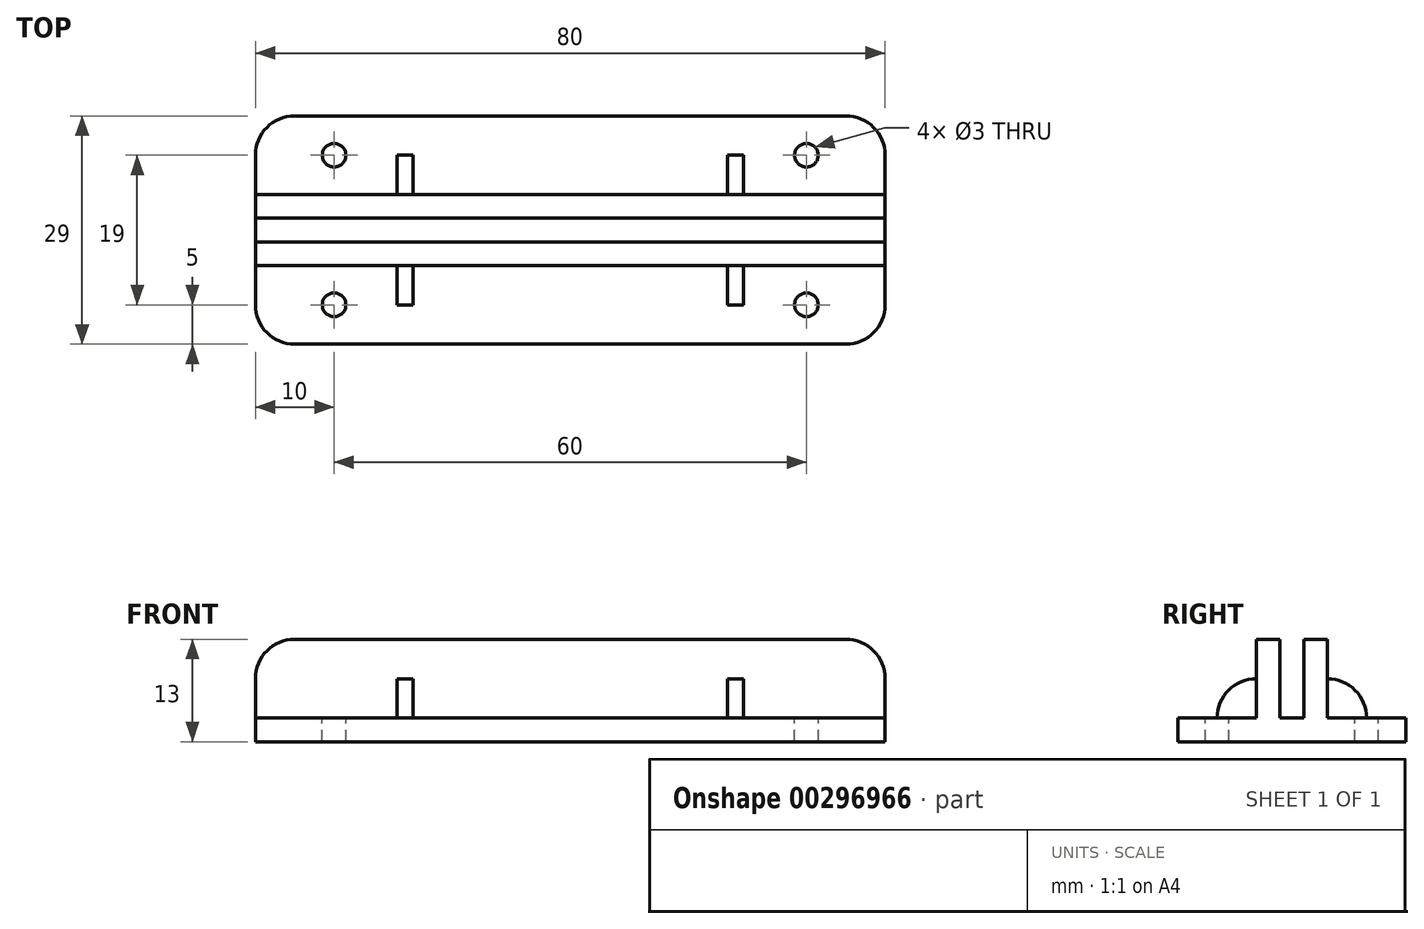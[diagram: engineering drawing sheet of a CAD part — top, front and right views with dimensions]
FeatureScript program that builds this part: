
annotation { "Feature Type Name" : "Feature", "Feature Type Description" : "" }
export const myFeature = defineFeature(function(context is Context, id is Id, definition is map)
    precondition{}
    {
        {
            var Q0;
            Q0=qCreatedBy(makeId("Top.planeOp"),FACE);
            var sketch = newSketch(context, id + "F0", { "sketchPlane" : qUnion([Q0])});
            skLineSegment(sketch, "E0.bottom", {"start": v(-40, 14.5) * mm, "end": v(40, 14.5) * mm});
            skLineSegment(sketch, "E0.top", {"start": v(-40, -14.5) * mm, "end": v(40, -14.5) * mm});
            skLineSegment(sketch, "E0.left", {"start": v(-40, 14.5) * mm, "end": v(-40, -14.5) * mm});
            skLineSegment(sketch, "E0.right", {"start": v(40, 14.5) * mm, "end": v(40, -14.5) * mm});
            skSolve(sketch);
        }
        {
            var Q0;
            Q0=makeQuery(id+"F0.imprint","IMPRINT",FACE,{"disambiguationData":[TD([[makeQuery(id+"F0.imprint","IMPRINT",EDGE,{"derivedFrom":sQuery(id+"F0.wireOp",EDGE,"E0.bottom")}),-1.0]])]});
            extrude(context, id + "F1", {"entities" : qUnion([Q0]), "depth" : 3 * mm});
        }
        {
            var Q0;
            Q0=makeQuery(id+"F1.opExtrude","CAP_FACE",FACE,{"disambiguationData":[OSD([sQuery(id+"F0.wireOp",EDGE,"E0.bottom"),sQuery(id+"F0.wireOp",EDGE,"E0.top"),sQuery(id+"F0.wireOp",EDGE,"E0.left"),sQuery(id+"F0.wireOp",EDGE,"E0.right")])],"isStart":false});
            var sketch = newSketch(context, id + "F2", { "sketchPlane" : qUnion([Q0])});
            skLineSegment(sketch, "E1.bottom", {"start": v(-40, 4.5) * mm, "end": v(40, 4.5) * mm});
            skLineSegment(sketch, "E1.top", {"start": v(-40, 1.5) * mm, "end": v(40, 1.5) * mm});
            skLineSegment(sketch, "E1.left", {"start": v(-40, 4.5) * mm, "end": v(-40, 1.5) * mm});
            skLineSegment(sketch, "E1.right", {"start": v(40, 4.5) * mm, "end": v(40, 1.5) * mm});
            skLineSegment(sketch, "E2.MirrorCS", {"start": v(40, -4.5) * mm, "end": v(40, -1.5) * mm});
            skLineSegment(sketch, "E3.MirrorCS", {"start": v(-40, -4.5) * mm, "end": v(-40, -1.5) * mm});
            skLineSegment(sketch, "E4.MirrorCS", {"start": v(-40, -1.5) * mm, "end": v(40, -1.5) * mm});
            skLineSegment(sketch, "E5.MirrorCS", {"start": v(-40, -4.5) * mm, "end": v(40, -4.5) * mm});
            skSolve(sketch);
        }
        {
            var Q0;
            Q0=makeQuery(id+"F2.imprint","IMPRINT",FACE,{"disambiguationData":[TD([[makeQuery(id+"F2.imprint","IMPRINT",EDGE,{"derivedFrom":sQuery(id+"F2.wireOp",EDGE,"E1.bottom")}),-1.0]])]});
            var Q1;
            Q1=makeQuery(id+"F2.imprint","IMPRINT",FACE,{"disambiguationData":[TD([[makeQuery(id+"F2.imprint","IMPRINT",EDGE,{"derivedFrom":sQuery(id+"F2.wireOp",EDGE,"E2.MirrorCS")}),-1.0]])]});
            extrude(context, id + "F3", {"entities" : qUnion([Q0, Q1]), "operationType" : NewBodyOperationType.ADD, "depth" : 10 * mm});
        }
        {
            var Q0;
            Q0=makeQuery(id+"F1.opExtrude","SWEPT_EDGE",EDGE,{"disambiguationData":[OSD([sQuery(id+"F0.wireOp",EDGE,"E0.bottom"),sQuery(id+"F0.wireOp",EDGE,"E0.right")])]});
            var Q1;
            Q1=makeQuery(id+"F1.opExtrude","SWEPT_EDGE",EDGE,{"disambiguationData":[OSD([sQuery(id+"F0.wireOp",EDGE,"E0.top"),sQuery(id+"F0.wireOp",EDGE,"E0.right")])]});
            var Q2;
            Q2=makeQuery(id+"F1.opExtrude","SWEPT_EDGE",EDGE,{"disambiguationData":[OSD([sQuery(id+"F0.wireOp",EDGE,"E0.bottom"),sQuery(id+"F0.wireOp",EDGE,"E0.left")])]});
            var Q3;
            Q3=makeQuery(id+"F1.opExtrude","SWEPT_EDGE",EDGE,{"disambiguationData":[OSD([sQuery(id+"F0.wireOp",EDGE,"E0.top"),sQuery(id+"F0.wireOp",EDGE,"E0.left")])]});
            var Q4;
            Q4=makeQuery(id+"F3.opExtrude","CAP_EDGE",EDGE,{"disambiguationData":[OSD([sQuery(id+"F2.wireOp",EDGE,"E1.right")])],"isStart":false});
            var Q5;
            Q5=makeQuery(id+"F3.opExtrude","CAP_EDGE",EDGE,{"disambiguationData":[OSD([sQuery(id+"F2.wireOp",EDGE,"E2.MirrorCS")])],"isStart":false});
            var Q6;
            Q6=makeQuery(id+"F3.opExtrude","CAP_EDGE",EDGE,{"disambiguationData":[OSD([sQuery(id+"F2.wireOp",EDGE,"E1.left")])],"isStart":false});
            var Q7;
            Q7=makeQuery(id+"F3.opExtrude","CAP_EDGE",EDGE,{"disambiguationData":[OSD([sQuery(id+"F2.wireOp",EDGE,"E3.MirrorCS")])],"isStart":false});
            fillet(context, id + "F4", {"entities" : qUnion([Q0, Q1, Q2, Q3, Q4, Q5, Q6, Q7]), "radius" : 5 * mm, "tangentPropagation" : true, "allowEdgeOverflow" : false});
        }
        {
            var Q0;
            {var subQ0=sQuery(id+"F0.wireOp",EDGE,"E0.left");var subQ1=sQuery(id+"F0.wireOp",EDGE,"E0.right");var subQ2=sQuery(id+"F0.wireOp",EDGE,"E0.bottom");Q0=makeQuery(id+"F3.boolean.opBoolean","SPLIT",FACE,{"disambiguationData":[TD([makeQuery(id+"F1.opExtrude","SWEPT_FACE",FACE,{"disambiguationData":[OSD([subQ2])]})])],"derivedFrom":makeQuery(id+"F1.opExtrude","CAP_FACE",FACE,{"disambiguationData":[OSD([subQ2,sQuery(id+"F0.wireOp",EDGE,"E0.top"),subQ0,subQ1])],"isStart":false})});}
            var sketch = newSketch(context, id + "F5", { "sketchPlane" : qUnion([Q0])});
            skCircle(sketch, "E6", {"center": v(-30, 9.5) * mm, "radius": 1.5 * mm});
            skCircle(sketch, "E7.MirrorC", {"center": v(30, 9.5) * mm, "radius": 1.5 * mm});
            skCircle(sketch, "E8.MirrorC", {"center": v(30, -9.5) * mm, "radius": 1.5 * mm});
            skCircle(sketch, "E9.MirrorC", {"center": v(-30, -9.5) * mm, "radius": 1.5 * mm});
            skSolve(sketch);
        }
        {
            var Q0;
            Q0=sQuery(id+"F5.wireOp",VERTEX,"E6.center");
            var Q1;
            Q1=sQuery(id+"F5.wireOp",VERTEX,"E9.MirrorC.center");
            var Q2;
            Q2=sQuery(id+"F5.wireOp",VERTEX,"E8.MirrorC.center");
            var Q3;
            Q3=sQuery(id+"F5.wireOp",VERTEX,"E7.MirrorC.center");
            var Q4;
            Q4=makeQuery(id+"F1.opExtrude","SWEPT_BODY",BODY,{"disambiguationData":[OSD([sQuery(id+"F0.wireOp",EDGE,"E0.bottom"),sQuery(id+"F0.wireOp",EDGE,"E0.top"),sQuery(id+"F0.wireOp",EDGE,"E0.left"),sQuery(id+"F0.wireOp",EDGE,"E0.right")])]});
            hole(context, id + "F6", {"style" : HoleStyle.SIMPLE, "endStyle" : HoleEndStyle.THROUGH, "holeDiameter" : 3 * mm, "tappedDepth" : 12 * mm, "tapClearance" : 3, "locations" : qUnion([Q0, Q1, Q2, Q3]), "scope" : qUnion([Q4])});
        }
        {
            var Q0;
            Q0=makeQuery(id+"F3.opExtrude","SWEPT_FACE",FACE,{"disambiguationData":[OSD([sQuery(id+"F2.wireOp",EDGE,"E5.MirrorCS")])]});
            var sketch = newSketch(context, id + "F7", { "sketchPlane" : qUnion([Q0])});
            skLineSegment(sketch, "E10.bottom", {"start": v(-22, 3) * mm, "end": v(-20, 3) * mm});
            skLineSegment(sketch, "E10.top", {"start": v(-22, 8) * mm, "end": v(-20, 8) * mm});
            skLineSegment(sketch, "E10.left", {"start": v(-22, 3) * mm, "end": v(-22, 8) * mm});
            skLineSegment(sketch, "E10.right", {"start": v(-20, 3) * mm, "end": v(-20, 8) * mm});
            skLineSegment(sketch, "E11.MirrorCS", {"start": v(22, 8) * mm, "end": v(20, 8) * mm});
            skLineSegment(sketch, "E12.MirrorCS", {"start": v(20, 3) * mm, "end": v(20, 8) * mm});
            skLineSegment(sketch, "E13.MirrorCS", {"start": v(22, 3) * mm, "end": v(22, 8) * mm});
            skLineSegment(sketch, "E14.MirrorCS", {"start": v(22, 3) * mm, "end": v(20, 3) * mm});
            skSolve(sketch);
        }
        {
            var Q0;
            Q0 = qSketchRegion(id + "F7", true);
            var Q1;
            Q1=sQuery(id+"F7.wireOp",EDGE,"E10.bottom");
            revolve(context, id + "F8", {"operationType" : NewBodyOperationType.ADD, "entities" : qUnion([Q0]), "axis" : qUnion([Q1]), "revolveType" : RevolveType.ONE_DIRECTION, "angle" : 90 * degree});
        }
        {
            var Q0;
            Q0=makeQuery(id+"F3.opExtrude","SWEPT_FACE",FACE,{"disambiguationData":[OSD([sQuery(id+"F2.wireOp",EDGE,"E1.bottom")])]});
            var sketch = newSketch(context, id + "F9", { "sketchPlane" : qUnion([Q0])});
            skLineSegment(sketch, "E15.bottom", {"start": v(-22, 3) * mm, "end": v(-20, 3) * mm});
            skLineSegment(sketch, "E15.top", {"start": v(-22, 8) * mm, "end": v(-20, 8) * mm});
            skLineSegment(sketch, "E15.left", {"start": v(-22, 3) * mm, "end": v(-22, 8) * mm});
            skLineSegment(sketch, "E15.right", {"start": v(-20, 3) * mm, "end": v(-20, 8) * mm});
            skLineSegment(sketch, "E16.MirrorCS", {"start": v(22, 8) * mm, "end": v(20, 8) * mm});
            skLineSegment(sketch, "E17.MirrorCS", {"start": v(22, 3) * mm, "end": v(20, 3) * mm});
            skLineSegment(sketch, "E18.MirrorCS", {"start": v(20, 3) * mm, "end": v(20, 8) * mm});
            skLineSegment(sketch, "E19.MirrorCS", {"start": v(22, 3) * mm, "end": v(22, 8) * mm});
            skSolve(sketch);
        }
        {
            var Q0;
            Q0=makeQuery(id+"F9.imprint","IMPRINT",FACE,{"disambiguationData":[TD([[makeQuery(id+"F9.imprint","IMPRINT",EDGE,{"derivedFrom":sQuery(id+"F9.wireOp",EDGE,"E15.bottom")}),-1.0]])]});
            var Q1;
            Q1=makeQuery(id+"F9.imprint","IMPRINT",FACE,{"disambiguationData":[TD([[makeQuery(id+"F9.imprint","IMPRINT",EDGE,{"derivedFrom":sQuery(id+"F9.wireOp",EDGE,"E16.MirrorCS")}),1.0]])]});
            var Q2;
            Q2=sQuery(id+"F9.wireOp",EDGE,"E15.bottom");
            revolve(context, id + "F10", {"operationType" : NewBodyOperationType.ADD, "entities" : qUnion([Q0, Q1]), "axis" : qUnion([Q2]), "revolveType" : RevolveType.ONE_DIRECTION, "angle" : 90 * degree});
        }
    });
